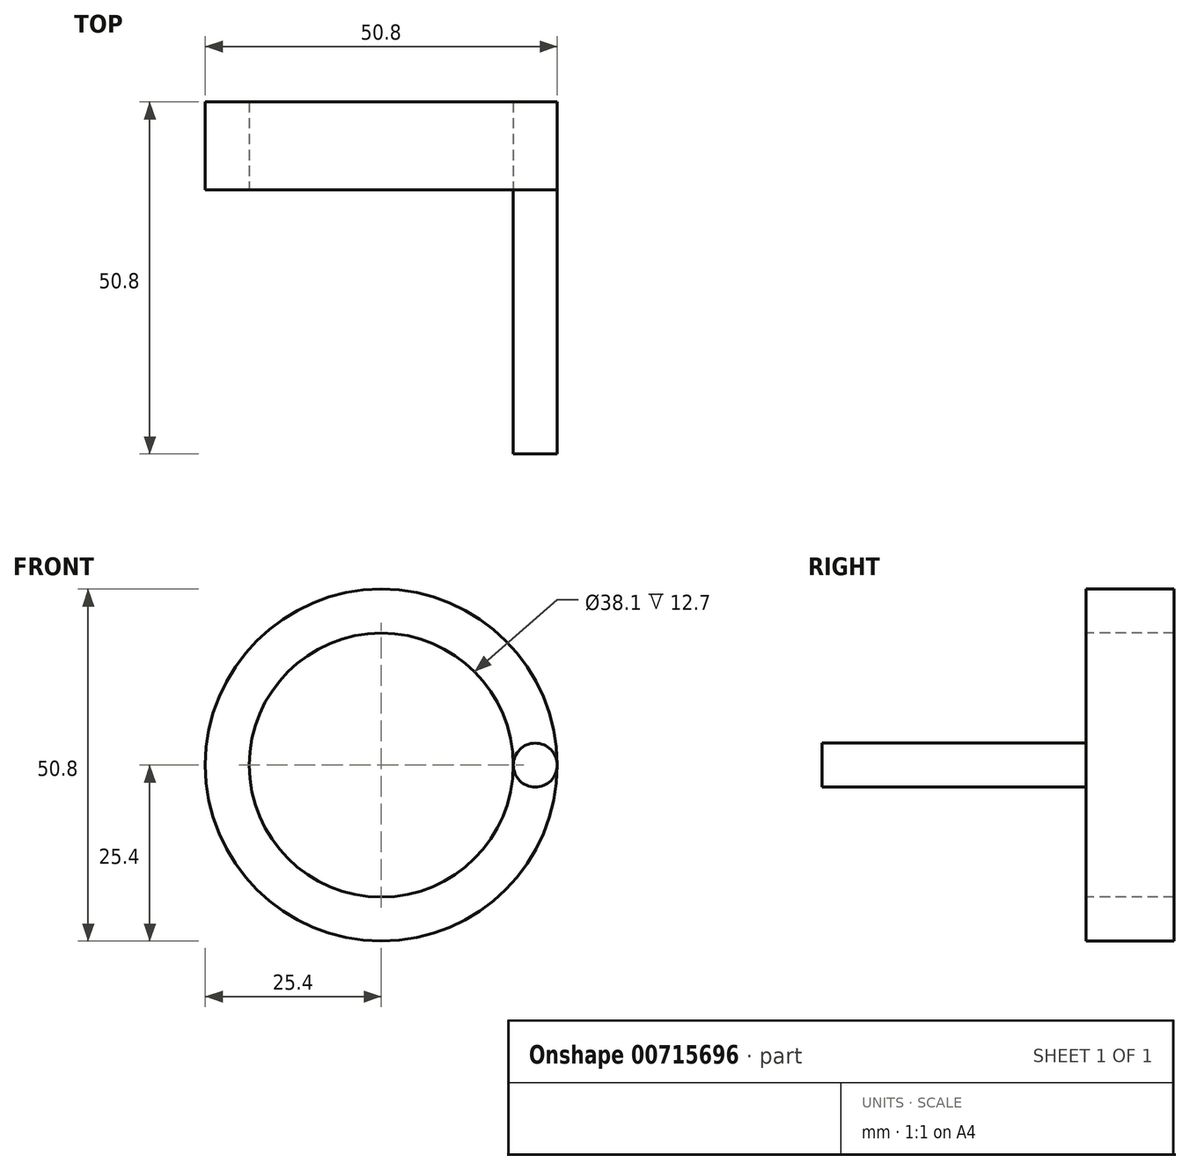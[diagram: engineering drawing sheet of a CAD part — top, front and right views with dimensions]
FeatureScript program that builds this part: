
annotation { "Feature Type Name" : "Feature", "Feature Type Description" : "" }
export const myFeature = defineFeature(function(context is Context, id is Id, definition is map)
    precondition{}
    {
        {
            var Q0;
            Q0=qCreatedBy(makeId("Front.planeOp"),FACE);
            var sketch = newSketch(context, id + "F0", { "sketchPlane" : qUnion([Q0])});
            skCircle(sketch, "E0", {"center": v(-25.4, 25.4) * mm, "radius": 25.4 * mm});
            skCircle(sketch, "E1", {"center": v(-25.4, 25.4) * mm, "radius": 19.05 * mm});
            skSolve(sketch);
        }
        {
            var Q0;
            Q0=makeQuery(id+"F0.imprint","IMPRINT",FACE,{"disambiguationData":[TD([[makeQuery(id+"F0.imprint","IMPRINT",EDGE,{"derivedFrom":sQuery(id+"F0.wireOp",EDGE,"E0")}),1.0]])]});
            extrude(context, id + "F1", {"entities" : qUnion([Q0]), "endBound" : BoundingType.SYMMETRIC, "oppositeDirection" : true, "depth" : 12.7 * mm, "offsetDistance" : 25.4 * mm});
        }
        {
            var Q0;
            Q0=makeQuery(id+"F1.opExtrude","CAP_FACE",FACE,{"disambiguationData":[OSD([sQuery(id+"F0.wireOp",EDGE,"E0"),sQuery(id+"F0.wireOp",EDGE,"E1")])],"isStart":true});
            var sketch = newSketch(context, id + "F2", { "sketchPlane" : qUnion([Q0])});
            skPoint(sketch, "E2", {"position": v(-3.18, 25.4) * mm});
            skCircle(sketch, "E3", {"center": v(-3.18, 25.4) * mm, "radius": 3.18 * mm});
            skSolve(sketch);
        }
        {
            var Q0;
            {var subQ0=sQuery(id+"F2.wireOp",EDGE,"E3");var subQ1=makeQuery(id+"F2.imprint","INTERSECT",VERTEX,{"derivedFrom":[makeQuery(id+"F1.opExtrude","CAP_EDGE",EDGE,{"disambiguationData":[OSD([sQuery(id+"F0.wireOp",EDGE,"E0")])],"isStart":true}),subQ0]});Q0=makeQuery(id+"F2.imprint","IMPRINT",FACE,{"disambiguationData":[TD([[makeQuery(id+"F2.imprint","IMPRINT",EDGE,{"disambiguationData":[TD([[subQ1,-1.0]])],"derivedFrom":subQ0}),1.0]])]});}
            extrude(context, id + "F3", {"entities" : qUnion([Q0]), "operationType" : NewBodyOperationType.ADD, "depth" : 38.1 * mm, "offsetDistance" : 25.4 * mm});
        }
    });
